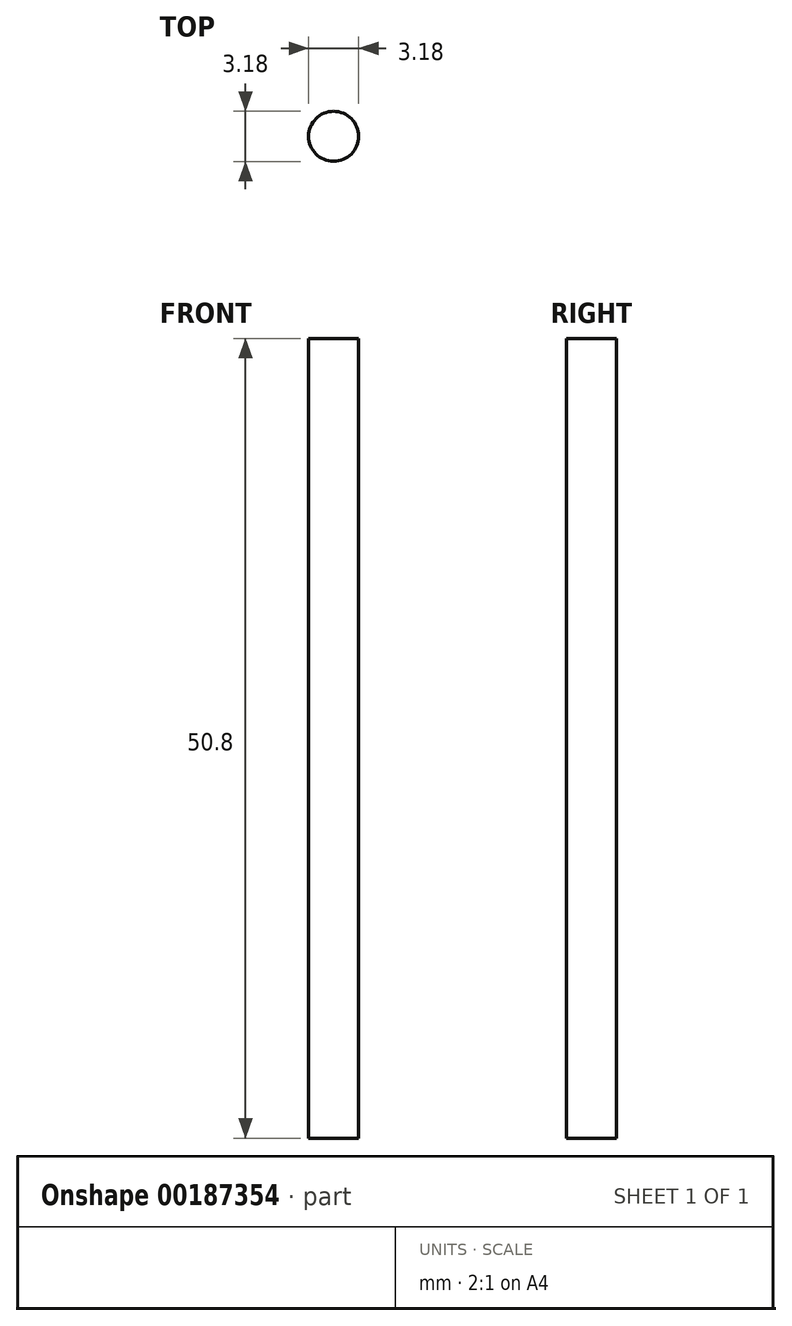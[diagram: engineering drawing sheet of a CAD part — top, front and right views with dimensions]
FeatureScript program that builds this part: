
annotation { "Feature Type Name" : "Feature", "Feature Type Description" : "" }
export const myFeature = defineFeature(function(context is Context, id is Id, definition is map)
    precondition{}
    {
        {
            var Q0;
            Q0=qCreatedBy(makeId("Top.planeOp"),FACE);
            var sketch = newSketch(context, id + "F0", { "sketchPlane" : qUnion([Q0])});
            skCircle(sketch, "E0", {"center": v(0, 0) * mm, "radius": 1.59 * mm});
            skSolve(sketch);
        }
        {
            var Q0;
            Q0 = qSketchRegion(id + "F0", true);
            extrude(context, id + "F1", {"entities" : qUnion([Q0]), "oppositeDirection" : true, "depth" : 50.8 * mm});
        }
    });
